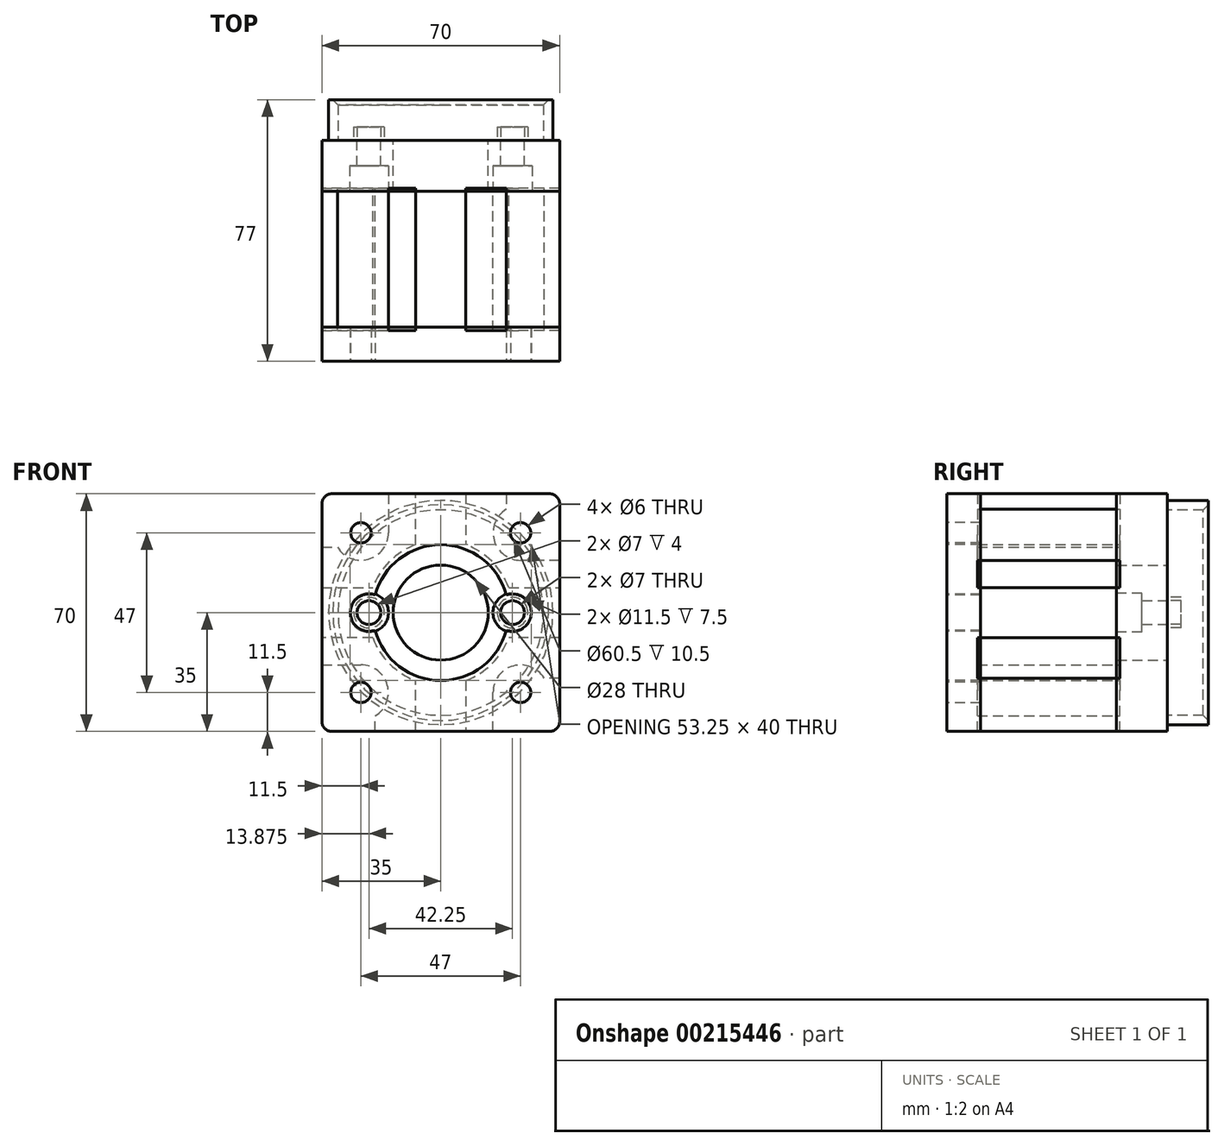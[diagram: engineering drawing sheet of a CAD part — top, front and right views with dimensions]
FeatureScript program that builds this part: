
annotation { "Feature Type Name" : "Feature", "Feature Type Description" : "" }
export const myFeature = defineFeature(function(context is Context, id is Id, definition is map)
    precondition{}
    {
        {
            var Q0;
            Q0=qCreatedBy(makeId("Front.planeOp"),FACE);
            var sketch = newSketch(context, id + "F0", { "sketchPlane" : qUnion([Q0])});
            skCircle(sketch, "E0", {"center": v(-21.12, 0) * mm, "radius": 4.5 * mm});
            skCircle(sketch, "E1", {"center": v(21.12, 0) * mm, "radius": 4.5 * mm});
            skCircle(sketch, "E2", {"center": v(-21.12, 0) * mm, "radius": 3.5 * mm});
            skCircle(sketch, "E3", {"center": v(21.12, 0) * mm, "radius": 3.5 * mm});
            skSolve(sketch);
        }
        {
            var Q0;
            Q0=makeQuery(id+"F0.imprint","IMPRINT",FACE,{"disambiguationData":[TD([[makeQuery(id+"F0.imprint","IMPRINT",EDGE,{"derivedFrom":sQuery(id+"F0.wireOp",EDGE,"E0")}),1.0]])]});
            var Q1;
            Q1=makeQuery(id+"F0.imprint","IMPRINT",FACE,{"disambiguationData":[TD([[makeQuery(id+"F0.imprint","IMPRINT",EDGE,{"derivedFrom":sQuery(id+"F0.wireOp",EDGE,"E1")}),1.0]])]});
            var Q2;
            Q2=sQuery(id+"F0.wireOp",EDGE,"E0");
            var Q3;
            Q3=sQuery(id+"F0.wireOp",EDGE,"E2");
            var Q4;
            Q4=sQuery(id+"F0.wireOp",EDGE,"E3");
            var Q5;
            Q5=sQuery(id+"F0.wireOp",EDGE,"E1");
            extrude(context, id + "F1", {"entities" : qUnion([Q0, Q1]), "surfaceEntities" : qUnion([Q2, Q3, Q4, Q5]), "oppositeDirection" : true, "depth" : 4 * mm});
        }
        {
            var Q0;
            Q0=qCreatedBy(makeId("Front.planeOp"),FACE);
            var sketch = newSketch(context, id + "F2", { "sketchPlane" : qUnion([Q0])});
            skCircle(sketch, "E4", {"center": v(0, 0) * mm, "radius": 33 * mm});
            skCircle(sketch, "E5", {"center": v(0, 0) * mm, "radius": 30.25 * mm});
            skSolve(sketch);
        }
        {
            var Q0;
            Q0=makeQuery(id+"F2.imprint","IMPRINT",FACE,{"disambiguationData":[TD([[makeQuery(id+"F2.imprint","IMPRINT",EDGE,{"derivedFrom":sQuery(id+"F2.wireOp",EDGE,"E4")}),1.0]])]});
            var Q1;
            Q1=sQuery(id+"F2.wireOp",EDGE,"E4");
            var Q2;
            Q2=sQuery(id+"F2.wireOp",EDGE,"E5");
            extrude(context, id + "F3", {"entities" : qUnion([Q0]), "surfaceEntities" : qUnion([Q1, Q2]), "oppositeDirection" : true, "depth" : 12 * mm});
        }
        {
            var Q0;
            Q0=makeQuery(id+"F3.opExtrude","CAP_EDGE",EDGE,{"disambiguationData":[OSD([sQuery(id+"F2.wireOp",EDGE,"E5")])],"isStart":false});
            chamfer(context, id + "F4", {"entities" : qUnion([Q0]), "width" : 1.5 * mm, "tangentPropagation" : true});
        }
        {
            var Q0;
            Q0=qCreatedBy(makeId("Front.planeOp"),FACE);
            var sketch = newSketch(context, id + "F5", { "sketchPlane" : qUnion([Q0])});
            skLineSegment(sketch, "E6.bottom", {"start": v(-35, 35) * mm, "end": v(35, 35) * mm});
            skLineSegment(sketch, "E6.top", {"start": v(-35, -35) * mm, "end": v(35, -35) * mm});
            skLineSegment(sketch, "E6.left", {"start": v(-35, 35) * mm, "end": v(-35, -35) * mm});
            skLineSegment(sketch, "E6.right", {"start": v(35, 35) * mm, "end": v(35, -35) * mm});
            skCircle(sketch, "E7", {"center": v(0, 0) * mm, "radius": 14 * mm});
            skCircle(sketch, "E8", {"center": v(21.12, 0) * mm, "radius": 3.5 * mm});
            skCircle(sketch, "E9", {"center": v(-21.12, 0) * mm, "radius": 3.5 * mm});
            skSolve(sketch);
        }
        {
            var Q0;
            Q0=qSketchRegion(id+"F5",true);
            extrude(context, id + "F6", {"entities" : qUnion([Q0]), "depth" : 15 * mm});
        }
        {
            var Q0;
            Q0=qCreatedBy(makeId("Front.planeOp"),FACE);
            cPlane(context, id + "F7", {"entities" : qUnion([Q0]), "cplaneType" : CPlaneType.OFFSET, "offset" : 15 * mm, "width" : 150 * mm, "height" : 150 * mm});
        }
        {
            var Q0;
            Q0=qCreatedBy(id+"F7.planeOp",FACE);
            var sketch = newSketch(context, id + "F8", { "sketchPlane" : qUnion([Q0])});
            skCircle(sketch, "E10", {"center": v(-21.12, 0) * mm, "radius": 5.75 * mm});
            skCircle(sketch, "E11", {"center": v(21.12, 0) * mm, "radius": 5.75 * mm});
            skSolve(sketch);
        }
        {
            var Q0;
            Q0=qSketchRegion(id+"F8",true);
            extrude(context, id + "F9", {"entities" : qUnion([Q0]), "operationType" : NewBodyOperationType.REMOVE, "oppositeDirection" : true, "depth" : 7.5 * mm});
        }
        {
            var Q0;
            Q0=qCreatedBy(makeId("Front.planeOp"),FACE);
            cPlane(context, id + "F10", {"entities" : qUnion([Q0]), "cplaneType" : CPlaneType.OFFSET, "offset" : 65 * mm, "width" : 150 * mm, "height" : 150 * mm});
        }
        {
            var Q0;
            Q0=qCreatedBy(id+"F10.planeOp",FACE);
            var sketch = newSketch(context, id + "F11", { "sketchPlane" : qUnion([Q0])});
            skLineSegment(sketch, "E12.bottom", {"start": v(-35, 35) * mm, "end": v(35, 35) * mm});
            skLineSegment(sketch, "E12.top", {"start": v(-35, -35) * mm, "end": v(35, -35) * mm});
            skLineSegment(sketch, "E12.left", {"start": v(-35, 35) * mm, "end": v(-35, -35) * mm});
            skLineSegment(sketch, "E12.right", {"start": v(35, 35) * mm, "end": v(35, -35) * mm});
            skCircle(sketch, "E13", {"center": v(0, 0) * mm, "radius": 20 * mm});
            skCircle(sketch, "E14", {"center": v(-23.5, 23.5) * mm, "radius": 3 * mm});
            skCircle(sketch, "E15", {"center": v(23.5, 23.5) * mm, "radius": 3 * mm});
            skCircle(sketch, "E16", {"center": v(-23.5, -23.5) * mm, "radius": 3 * mm});
            skCircle(sketch, "E17", {"center": v(23.5, -23.5) * mm, "radius": 3 * mm});
            skCircle(sketch, "E18", {"center": v(-21.12, 0) * mm, "radius": 5.5 * mm});
            skCircle(sketch, "E19", {"center": v(21.12, 0) * mm, "radius": 5.5 * mm});
            skSolve(sketch);
        }
        {
            var Q0;
            Q0=qSketchRegion(id+"F11",true);
            extrude(context, id + "F12", {"entities" : qUnion([Q0]), "oppositeDirection" : true, "depth" : 10 * mm});
        }
        {
            var Q0;
            Q0=qCreatedBy(makeId("Front.planeOp"),FACE);
            cPlane(context, id + "F13", {"entities" : qUnion([Q0]), "cplaneType" : CPlaneType.OFFSET, "offset" : 14 * mm, "width" : 150 * mm, "height" : 150 * mm});
        }
        {
            var Q0;
            Q0=qCreatedBy(id+"F13.planeOp",FACE);
            var sketch = newSketch(context, id + "F14", { "sketchPlane" : qUnion([Q0])});
            skArc(sketch, "E20", {"start": v(-15.4, 23.5) * mm, "mid": v(-21.31, 15.7) * mm, "end": v(-30.4, 19.28) * mm});
            skLineSegment(sketch, "E21", {"start": v(-35, 19.28) * mm, "end": v(-30.4, 19.28) * mm});
            skPoint(sketch, "E22.center", {"position": v(0, 0) * mm});
            skLineSegment(sketch, "E23", {"start": v(-7.4, 20) * mm, "end": v(-7.4, 35) * mm});
            skLineSegment(sketch, "E24", {"start": v(-7.4, 35) * mm, "end": v(-15.4, 35) * mm});
            skLineSegment(sketch, "E25", {"start": v(-15.4, 35) * mm, "end": v(-15.4, 23.5) * mm});
            skLineSegment(sketch, "E26", {"start": v(-35, 7.4) * mm, "end": v(-20, 7.4) * mm});
            skLineSegment(sketch, "E27", {"start": v(-35, 19.28) * mm, "end": v(-35, 7.4) * mm});
            skArc(sketch, "E28", {"start": v(-7.4, 20) * mm, "mid": v(-15.07, 15.07) * mm, "end": v(-20, 7.4) * mm});
            skLineSegment(sketch, "E29.1.0", {"start": v(-35, -7.4) * mm, "end": v(-35, -15.4) * mm});
            skLineSegment(sketch, "E29.1.1", {"start": v(-20, -7.4) * mm, "end": v(-35, -7.4) * mm});
            skArc(sketch, "E29.1.2", {"start": v(-20, -7.4) * mm, "mid": v(-15.07, -15.07) * mm, "end": v(-7.4, -20) * mm});
            skLineSegment(sketch, "E29.1.3", {"start": v(-7.4, -35) * mm, "end": v(-7.4, -20) * mm});
            skLineSegment(sketch, "E29.1.4", {"start": v(-19.28, -35) * mm, "end": v(-7.4, -35) * mm});
            skLineSegment(sketch, "E29.1.5", {"start": v(-19.28, -35) * mm, "end": v(-19.28, -30.4) * mm});
            skArc(sketch, "E29.1.6", {"start": v(-23.5, -15.4) * mm, "mid": v(-15.7, -21.31) * mm, "end": v(-19.28, -30.4) * mm});
            skLineSegment(sketch, "E29.1.7", {"start": v(-35, -15.4) * mm, "end": v(-23.5, -15.4) * mm});
            skLineSegment(sketch, "E29.2.0", {"start": v(7.4, -35) * mm, "end": v(15.4, -35) * mm});
            skLineSegment(sketch, "E29.2.1", {"start": v(7.4, -20) * mm, "end": v(7.4, -35) * mm});
            skArc(sketch, "E29.2.2", {"start": v(7.4, -20) * mm, "mid": v(15.07, -15.07) * mm, "end": v(20, -7.4) * mm});
            skLineSegment(sketch, "E29.2.3", {"start": v(35, -7.4) * mm, "end": v(20, -7.4) * mm});
            skLineSegment(sketch, "E29.2.4", {"start": v(35, -19.28) * mm, "end": v(35, -7.4) * mm});
            skLineSegment(sketch, "E29.2.5", {"start": v(35, -19.28) * mm, "end": v(30.4, -19.28) * mm});
            skArc(sketch, "E29.2.6", {"start": v(15.4, -23.5) * mm, "mid": v(21.31, -15.7) * mm, "end": v(30.4, -19.28) * mm});
            skLineSegment(sketch, "E29.2.7", {"start": v(15.4, -35) * mm, "end": v(15.4, -23.5) * mm});
            skLineSegment(sketch, "E29.3.0", {"start": v(35, 7.4) * mm, "end": v(35, 15.4) * mm});
            skLineSegment(sketch, "E29.3.1", {"start": v(20, 7.4) * mm, "end": v(35, 7.4) * mm});
            skArc(sketch, "E29.3.2", {"start": v(20, 7.4) * mm, "mid": v(15.07, 15.07) * mm, "end": v(7.4, 20) * mm});
            skLineSegment(sketch, "E29.3.3", {"start": v(7.4, 35) * mm, "end": v(7.4, 20) * mm});
            skLineSegment(sketch, "E29.3.4", {"start": v(19.28, 35) * mm, "end": v(7.4, 35) * mm});
            skLineSegment(sketch, "E29.3.5", {"start": v(19.28, 35) * mm, "end": v(19.28, 30.4) * mm});
            skArc(sketch, "E29.3.6", {"start": v(23.5, 15.4) * mm, "mid": v(15.7, 21.31) * mm, "end": v(19.28, 30.4) * mm});
            skLineSegment(sketch, "E29.3.7", {"start": v(35, 15.4) * mm, "end": v(23.5, 15.4) * mm});
            skSolve(sketch);
        }
        {
            var Q0;
            Q0=qSketchRegion(id+"F14",true);
            extrude(context, id + "F15", {"entities" : qUnion([Q0]), "depth" : 42 * mm});
        }
        {
            var Q0;
            Q0=makeQuery(id+"F12.opExtrude","SWEPT_EDGE",EDGE,{"disambiguationData":[OSD([sQuery(id+"F11.wireOp",EDGE,"E12.bottom"),sQuery(id+"F11.wireOp",EDGE,"E12.left")])]});
            var Q1;
            Q1=makeQuery(id+"F12.opExtrude","SWEPT_EDGE",EDGE,{"disambiguationData":[OSD([sQuery(id+"F11.wireOp",EDGE,"E12.bottom"),sQuery(id+"F11.wireOp",EDGE,"E12.right")])]});
            var Q2;
            Q2=makeQuery(id+"F12.opExtrude","SWEPT_EDGE",EDGE,{"disambiguationData":[OSD([sQuery(id+"F11.wireOp",EDGE,"E12.top"),sQuery(id+"F11.wireOp",EDGE,"E12.right")])]});
            var Q3;
            Q3=makeQuery(id+"F12.opExtrude","SWEPT_EDGE",EDGE,{"disambiguationData":[OSD([sQuery(id+"F11.wireOp",EDGE,"E12.top"),sQuery(id+"F11.wireOp",EDGE,"E12.left")])]});
            fillet(context, id + "F16", {"entities" : qUnion([Q0, Q1, Q2, Q3]), "radius" : 3 * mm, "tangentPropagation" : true, "allowEdgeOverflow" : false});
        }
        {
            var Q0;
            Q0=makeQuery(id+"F6.opExtrude","SWEPT_EDGE",EDGE,{"disambiguationData":[OSD([sQuery(id+"F5.wireOp",EDGE,"E6.top"),sQuery(id+"F5.wireOp",EDGE,"E6.right")])]});
            var Q1;
            Q1=makeQuery(id+"F6.opExtrude","SWEPT_EDGE",EDGE,{"disambiguationData":[OSD([sQuery(id+"F5.wireOp",EDGE,"E6.bottom"),sQuery(id+"F5.wireOp",EDGE,"E6.right")])]});
            var Q2;
            Q2=makeQuery(id+"F6.opExtrude","SWEPT_EDGE",EDGE,{"disambiguationData":[OSD([sQuery(id+"F5.wireOp",EDGE,"E6.bottom"),sQuery(id+"F5.wireOp",EDGE,"E6.left")])]});
            var Q3;
            Q3=makeQuery(id+"F6.opExtrude","SWEPT_EDGE",EDGE,{"disambiguationData":[OSD([sQuery(id+"F5.wireOp",EDGE,"E6.top"),sQuery(id+"F5.wireOp",EDGE,"E6.left")])]});
            fillet(context, id + "F17", {"entities" : qUnion([Q0, Q1, Q2, Q3]), "radius" : 3 * mm, "tangentPropagation" : true, "allowEdgeOverflow" : false});
        }
    });
